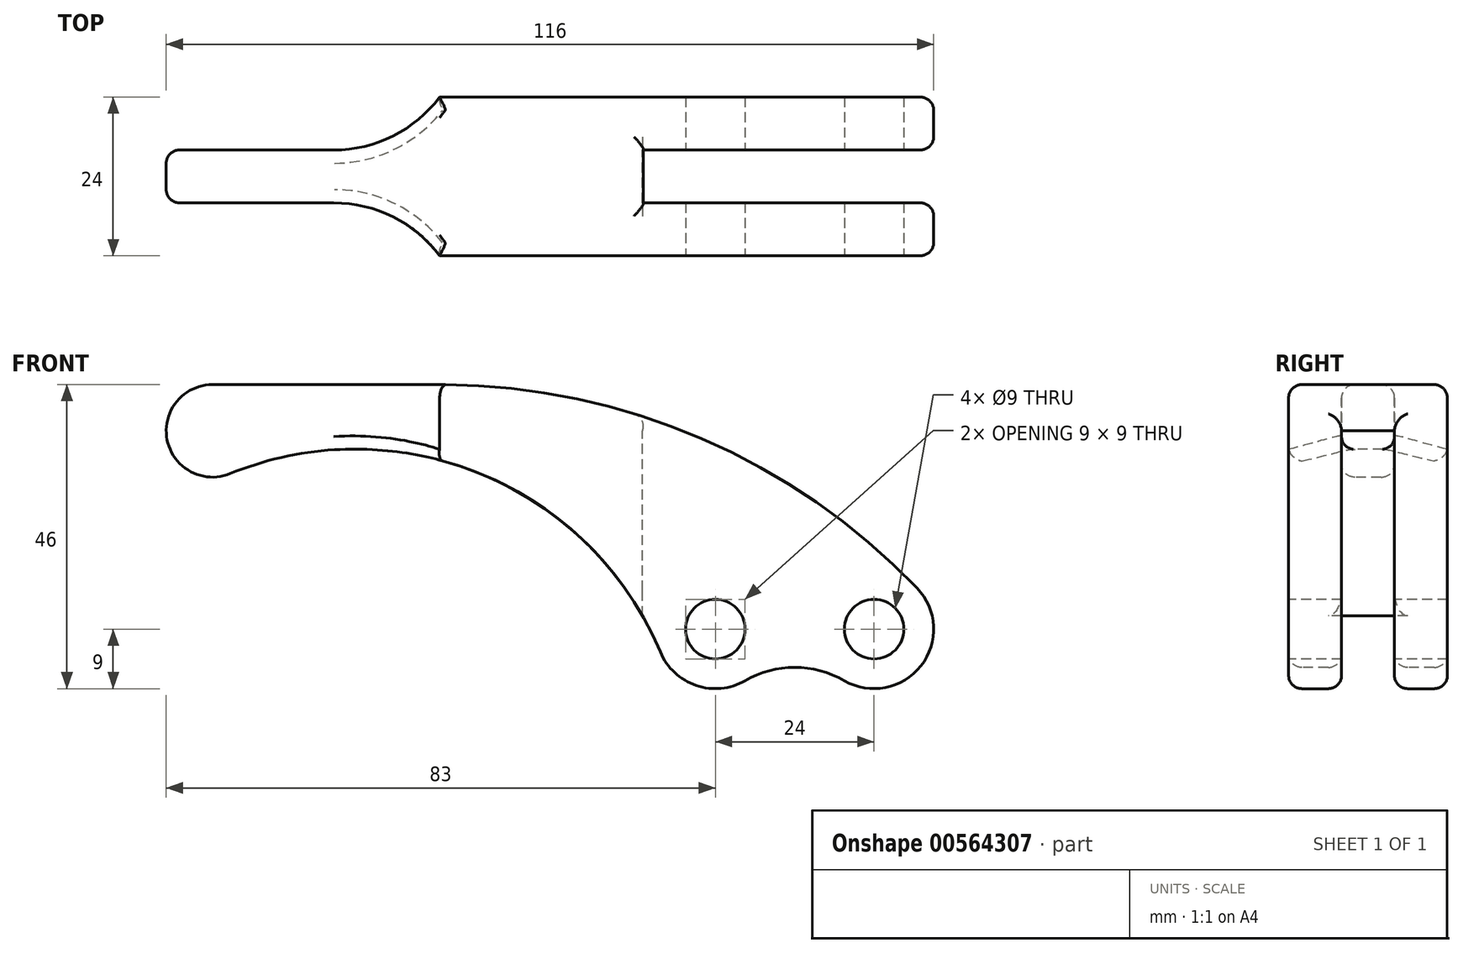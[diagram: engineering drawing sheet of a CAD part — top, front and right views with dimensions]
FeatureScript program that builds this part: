
annotation { "Feature Type Name" : "Feature", "Feature Type Description" : "" }
export const myFeature = defineFeature(function(context is Context, id is Id, definition is map)
    precondition{}
    {
        {
            var Q0;
            Q0=qCreatedBy(makeId("Front.planeOp"),FACE);
            var sketch = newSketch(context, id + "F0", { "sketchPlane" : qUnion([Q0])});
            skArc(sketch, "E0", {"start": v(0, 7) * mm, "mid": v(-6.87, -1.35) * mm, "end": v(2.65, -6.48) * mm});
            skCircle(sketch, "E1", {"center": v(100, -30) * mm, "radius": 4.5 * mm});
            skCircle(sketch, "E2", {"center": v(76, -30) * mm, "radius": 4.5 * mm});
            skArc(sketch, "E3", {"start": v(67.7, -33.47) * mm, "mid": v(73.12, -38.53) * mm, "end": v(80.5, -37.8) * mm});
            skArc(sketch, "E4", {"start": v(95.5, -37.8) * mm, "mid": v(107.08, -35.55) * mm, "end": v(106.5, -23.77) * mm});
            skArc(sketch, "E5", {"start": v(95.5, -37.8) * mm, "mid": v(88, -35.78) * mm, "end": v(80.5, -37.8) * mm});
            skArc(sketch, "E6", {"start": v(67.7, -33.47) * mm, "mid": v(40.73, -6.58) * mm, "end": v(2.65, -6.48) * mm});
            skLineSegment(sketch, "E7", {"start": v(0, 7) * mm, "end": v(34.33, 7) * mm});
            skArc(sketch, "E8", {"start": v(106.5, -23.77) * mm, "mid": v(73.56, -1.01) * mm, "end": v(34.33, 7) * mm});
            skSolve(sketch);
        }
        {
            var Q0;
            Q0=makeQuery(id+"F0.imprint","IMPRINT",FACE,{"disambiguationData":[TD([[makeQuery(id+"F0.imprint","IMPRINT",EDGE,{"derivedFrom":sQuery(id+"F0.wireOp",EDGE,"E0")}),1.0]])]});
            extrude(context, id + "F1", {"entities" : qUnion([Q0]), "oppositeDirection" : true, "depth" : 24 * mm, "offsetDistance" : 25 * mm});
        }
        {
            var Q0;
            Q0=qCreatedBy(makeId("Top.planeOp"),FACE);
            var sketch = newSketch(context, id + "F2", { "sketchPlane" : qUnion([Q0])});
            skLineSegment(sketch, "E9.0", {"start": v(0, 0) * mm, "end": v(34.33, 0) * mm, "construction": true});
            skLineSegment(sketch, "E10", {"start": v(-7, 0) * mm, "end": v(-7, 24) * mm, "construction": true});
            skLineSegment(sketch, "E11", {"start": v(-7, 8) * mm, "end": v(18.33, 8) * mm});
            skArc(sketch, "E12", {"start": v(34.33, 0) * mm, "mid": v(27.28, 5.89) * mm, "end": v(18.33, 8) * mm});
            skLineSegment(sketch, "E13", {"start": v(-7, 8) * mm, "end": v(-7, 0) * mm});
            skLineSegment(sketch, "E14", {"start": v(-7, 0) * mm, "end": v(2.33, 0) * mm});
            skLineSegment(sketch, "E15", {"start": v(-7, 0) * mm, "end": v(34.33, 0) * mm});
            skLineSegment(sketch, "E16", {"start": v(-7, 12) * mm, "end": v(150.93, 12) * mm});
            skArc(sketch, "E17.MirrorCS", {"start": v(34.33, 24) * mm, "mid": v(27.28, 18.11) * mm, "end": v(18.33, 16) * mm});
            skLineSegment(sketch, "E18.MirrorCS", {"start": v(0, 24) * mm, "end": v(34.33, 24) * mm, "construction": true});
            skLineSegment(sketch, "E19.MirrorCS", {"start": v(-7, 16) * mm, "end": v(18.33, 16) * mm});
            skLineSegment(sketch, "E20.MirrorCS", {"start": v(-7, 24) * mm, "end": v(34.33, 24) * mm});
            skLineSegment(sketch, "E21", {"start": v(-7, 16) * mm, "end": v(-7, 24) * mm});
            skSolve(sketch);
        }
        {
            var Q0;
            Q0 = qSketchRegion(id + "F2", true);
            extrude(context, id + "F3", {"entities" : qUnion([Q0]), "operationType" : NewBodyOperationType.REMOVE, "oppositeDirection" : true, "depth" : 25 * mm, "offsetDistance" : 25 * mm, "hasSecondDirection" : true, "secondDirectionOppositeDirection" : false, "secondDirectionDepth" : 25 * mm});
        }
        {
            var Q0;
            Q0=qCreatedBy(makeId("Top.planeOp"),FACE);
            var sketch = newSketch(context, id + "F4", { "sketchPlane" : qUnion([Q0])});
            skLineSegment(sketch, "E22.0", {"start": v(104.5, 0) * mm, "end": v(95.5, 0) * mm, "construction": true});
            skLineSegment(sketch, "E23", {"start": v(100, 8) * mm, "end": v(65, 8) * mm});
            skPoint(sketch, "E23.startSnap0", {"position": v(100, 0) * mm});
            skLineSegment(sketch, "E24", {"start": v(65, 8) * mm, "end": v(65, 16) * mm});
            skLineSegment(sketch, "E25", {"start": v(65, 16) * mm, "end": v(100, 16) * mm});
            skLineSegment(sketch, "E26", {"start": v(109, 24) * mm, "end": v(109, 0) * mm, "construction": true});
            skLineSegment(sketch, "E27", {"start": v(100, 8) * mm, "end": v(109, 8) * mm});
            skLineSegment(sketch, "E28", {"start": v(109, 8) * mm, "end": v(109, 16) * mm, "construction": true});
            skPoint(sketch, "E28.endSnap0", {"position": v(109, 12) * mm});
            skLineSegment(sketch, "E29", {"start": v(109, 16) * mm, "end": v(100, 16) * mm});
            skLineSegment(sketch, "E30", {"start": v(109, 8) * mm, "end": v(109, 16) * mm});
            skSolve(sketch);
        }
        {
            var Q0;
            Q0 = qSketchRegion(id + "F4", true);
            extrude(context, id + "F5", {"entities" : qUnion([Q0]), "operationType" : NewBodyOperationType.REMOVE, "endBound" : BoundingType.THROUGH_ALL, "oppositeDirection" : true, "depth" : 25 * mm, "offsetDistance" : 25 * mm});
        }
        {
            var Q0;
            Q0=makeQuery(id+"F1.opExtrude","CAP_EDGE",EDGE,{"disambiguationData":[OSD([sQuery(id+"F0.wireOp",EDGE,"E8")])],"isStart":false});
            var Q1;
            Q1=makeQuery(id+"F3.boolean.opBoolean","INTERSECT",EDGE,{"derivedFrom":[makeQuery(id+"F1.opExtrude","SWEPT_FACE",FACE,{"disambiguationData":[OSD([sQuery(id+"F0.wireOp",EDGE,"E7")])]}),makeQuery(id+"F3.opExtrude","SWEPT_FACE",FACE,{"disambiguationData":[OSD([sQuery(id+"F2.wireOp",EDGE,"E17.MirrorCS")])]})]});
            var Q2;
            Q2=makeQuery(id+"F1.opExtrude","CAP_EDGE",EDGE,{"disambiguationData":[OSD([sQuery(id+"F0.wireOp",EDGE,"E8")])],"isStart":true});
            var Q3;
            Q3=makeQuery(id+"F3.boolean.opBoolean","INTERSECT",EDGE,{"derivedFrom":[makeQuery(id+"F1.opExtrude","SWEPT_FACE",FACE,{"disambiguationData":[OSD([sQuery(id+"F0.wireOp",EDGE,"E7")])]}),makeQuery(id+"F3.opExtrude","SWEPT_FACE",FACE,{"disambiguationData":[OSD([sQuery(id+"F2.wireOp",EDGE,"E12")])]})]});
            var Q4;
            Q4=makeQuery(id+"F5.boolean.opBoolean","INTERSECT",EDGE,{"derivedFrom":[makeQuery(id+"F1.opExtrude","SWEPT_FACE",FACE,{"disambiguationData":[OSD([sQuery(id+"F0.wireOp",EDGE,"E8")])]}),makeQuery(id+"F5.opExtrude","CAP_FACE",FACE,{"disambiguationData":[OSD([sQuery(id+"F4.wireOp",EDGE,"E23"),sQuery(id+"F4.wireOp",EDGE,"E24"),sQuery(id+"F4.wireOp",EDGE,"E25"),sQuery(id+"F4.wireOp",EDGE,"E27"),sQuery(id+"F4.wireOp",EDGE,"E29"),sQuery(id+"F4.wireOp",EDGE,"E30")])],"isStart":true})]});
            var Q5;
            Q5=makeQuery(id+"F5.boolean.opBoolean","INTERSECT",EDGE,{"derivedFrom":[makeQuery(id+"F1.opExtrude","SWEPT_FACE",FACE,{"disambiguationData":[OSD([sQuery(id+"F0.wireOp",EDGE,"E8")])]}),makeQuery(id+"F5.opExtrude","SWEPT_FACE",FACE,{"disambiguationData":[OSD([sQuery(id+"F4.wireOp",EDGE,"E23"),sQuery(id+"F4.wireOp",EDGE,"E27")])]})]});
            var Q6;
            Q6=makeQuery(id+"F5.boolean.opBoolean","INTERSECT",EDGE,{"derivedFrom":[makeQuery(id+"F1.opExtrude","SWEPT_FACE",FACE,{"disambiguationData":[OSD([sQuery(id+"F0.wireOp",EDGE,"E8")])]}),makeQuery(id+"F5.opExtrude","SWEPT_FACE",FACE,{"disambiguationData":[OSD([sQuery(id+"F4.wireOp",EDGE,"E25"),sQuery(id+"F4.wireOp",EDGE,"E29")])]})]});
            fillet(context, id + "F6", {"entities" : qUnion([Q0, Q1, Q2, Q3, Q4, Q5, Q6]), "radius" : 2 * mm, "tangentPropagation" : true, "allowEdgeOverflow" : false});
        }
    });
